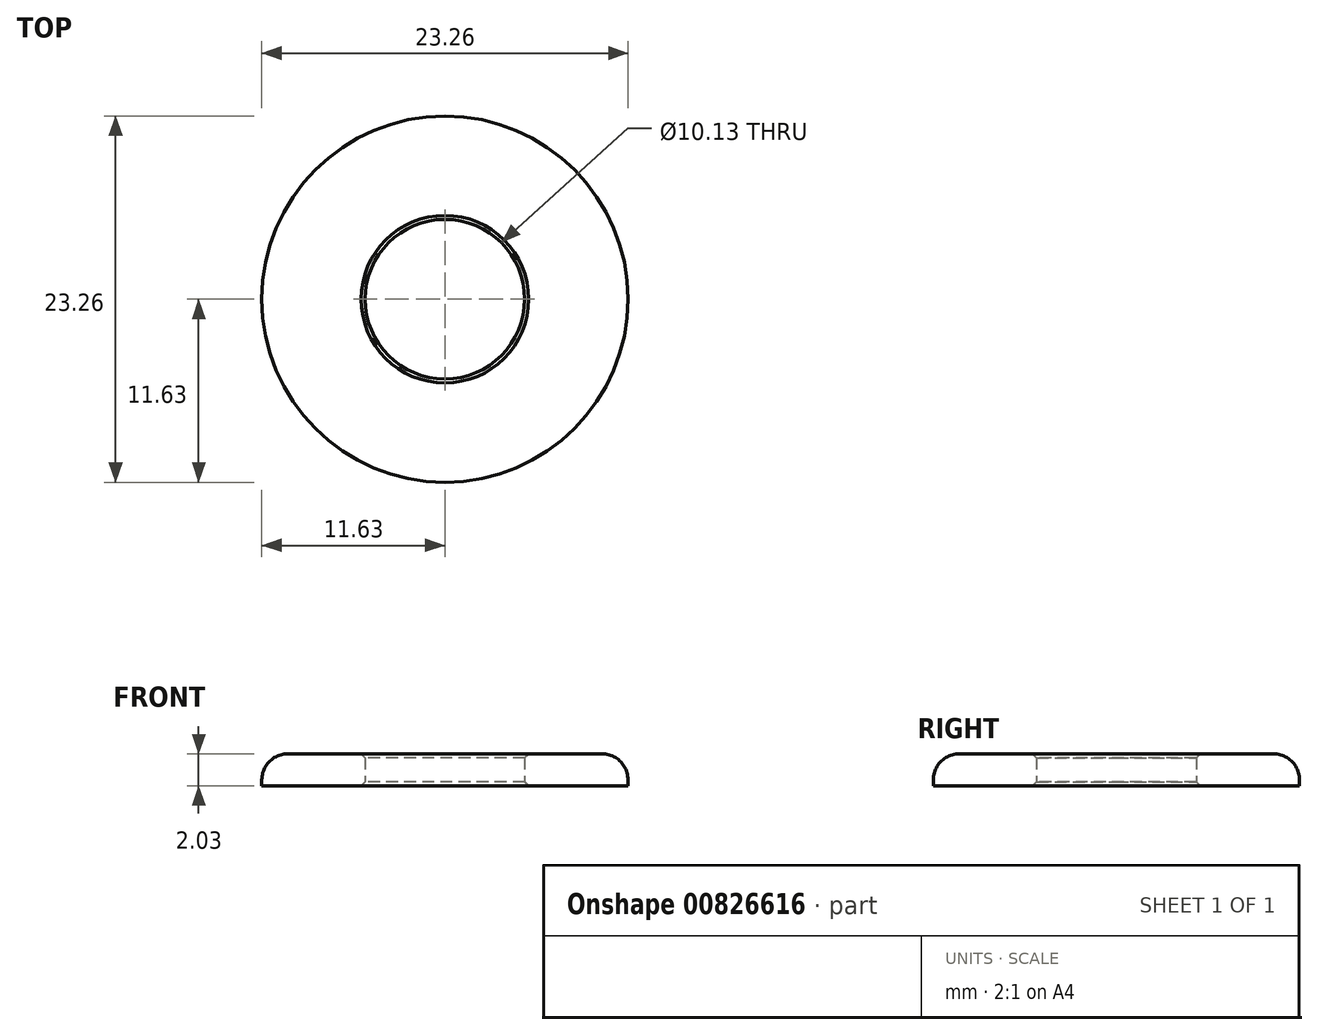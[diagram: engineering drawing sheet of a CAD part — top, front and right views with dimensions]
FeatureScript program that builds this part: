
annotation { "Feature Type Name" : "Feature", "Feature Type Description" : "" }
export const myFeature = defineFeature(function(context is Context, id is Id, definition is map)
    precondition{}
    {
        {
            var Q0;
            Q0=qCreatedBy(makeId("Top.planeOp"),FACE);
            var sketch = newSketch(context, id + "F0", { "sketchPlane" : qUnion([Q0])});
            skCircle(sketch, "E0", {"center": v(0, 0) * mm, "radius": 11.63 * mm});
            skCircle(sketch, "E1", {"center": v(0, 0) * mm, "radius": 5.07 * mm});
            skLineSegment(sketch, "E2", {"start": v(-1.33, 9.9) * mm, "end": v(1.37, 9.9) * mm});
            skSolve(sketch);
        }
        {
            var Q0;
            Q0 = qSketchRegion(id + "F0", true);
            extrude(context, id + "F1", {"entities" : qUnion([Q0]), "depth" : 2.03 * mm, "offsetDistance" : 25.4 * mm});
        }
        {
            var Q0;
            Q0=makeQuery(id+"F1.opExtrude","CAP_EDGE",EDGE,{"disambiguationData":[OSD([sQuery(id+"F0.wireOp",EDGE,"E0")])],"isStart":false});
            fillet(context, id + "F2", {"entities" : qUnion([Q0]), "radius" : 1.65 * mm, "tangentPropagation" : true, "allowEdgeOverflow" : false});
        }
        {
            var Q0;
            Q0=makeQuery(id+"F1.opExtrude","CAP_EDGE",EDGE,{"disambiguationData":[OSD([sQuery(id+"F0.wireOp",EDGE,"E1")])],"isStart":false});
            chamfer(context, id + "F3", {"entities" : qUnion([Q0]), "width" : 0.25 * mm, "tangentPropagation" : true});
        }
        {
            var Q0;
            Q0=makeQuery(id+"F1.opExtrude","CAP_EDGE",EDGE,{"disambiguationData":[OSD([sQuery(id+"F0.wireOp",EDGE,"E1")])],"isStart":true});
            chamfer(context, id + "F4", {"entities" : qUnion([Q0]), "width" : 0.25 * mm, "tangentPropagation" : true});
        }
    });
